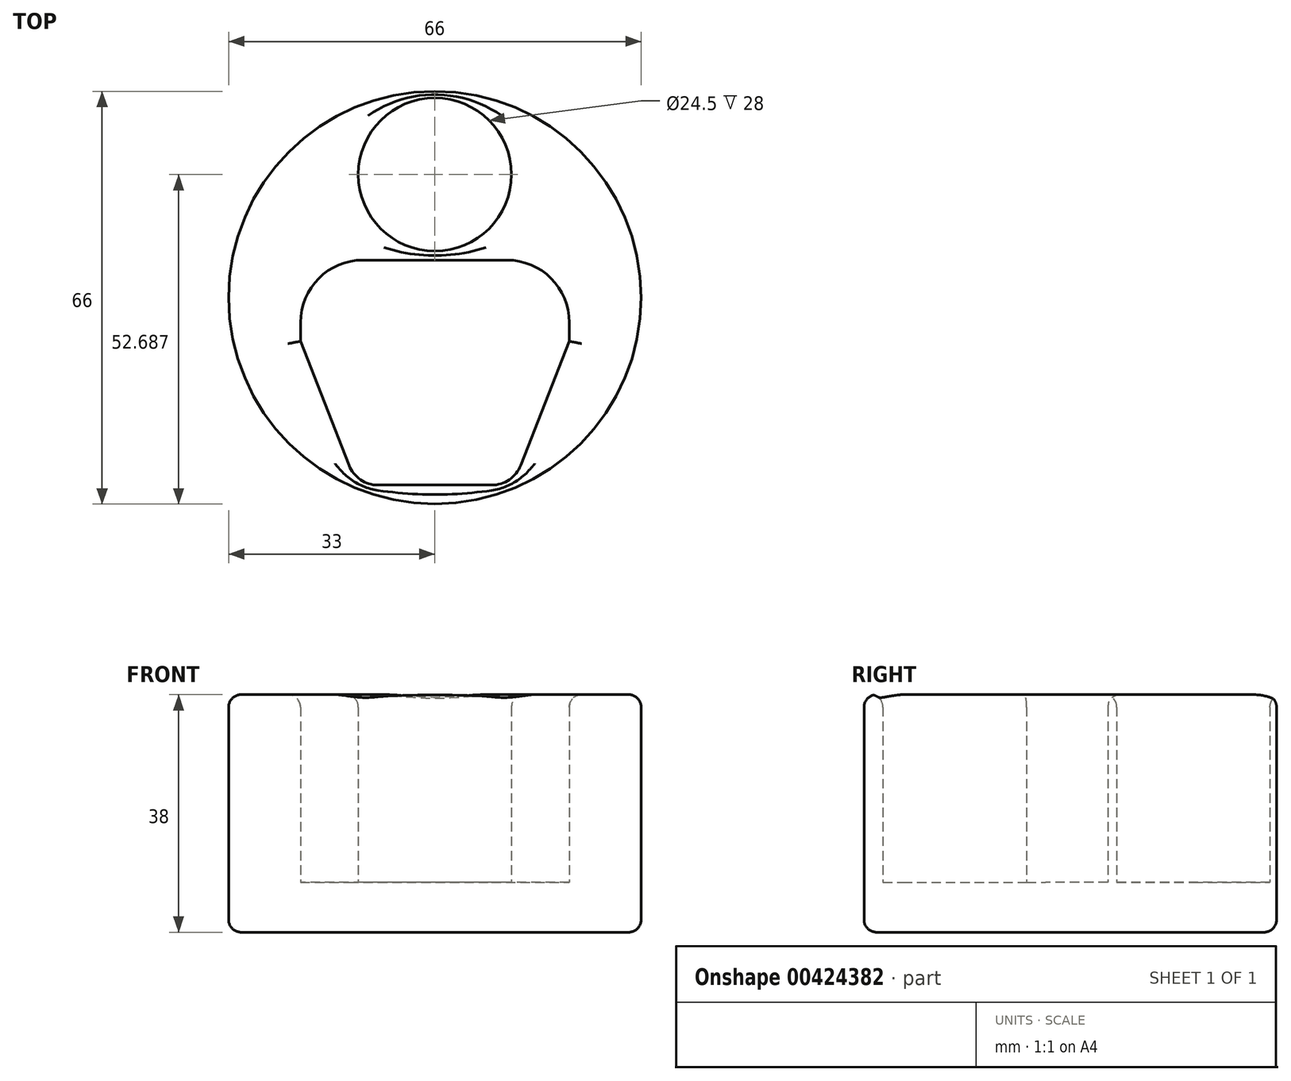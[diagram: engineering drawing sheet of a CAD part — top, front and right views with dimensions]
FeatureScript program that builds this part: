
annotation { "Feature Type Name" : "Feature", "Feature Type Description" : "" }
export const myFeature = defineFeature(function(context is Context, id is Id, definition is map)
    precondition{}
    {
        {
            var Q0;
            Q0=qCreatedBy(makeId("Top.planeOp"),FACE);
            var sketch = newSketch(context, id + "F0", { "sketchPlane" : qUnion([Q0])});
            skCircle(sketch, "E0", {"center": v(0, 0) * mm, "radius": 33 * mm});
            skCircle(sketch, "E1", {"center": v(0, 19.69) * mm, "radius": 12.25 * mm});
            skLineSegment(sketch, "E2", {"start": v(-9.09, -29.99) * mm, "end": v(9.09, -29.99) * mm});
            skLineSegment(sketch, "E3", {"start": v(13.74, -26.81) * mm, "end": v(21.5, -6.99) * mm});
            skLineSegment(sketch, "E4", {"start": v(21.5, -6.99) * mm, "end": v(21.5, -3.99) * mm});
            skLineSegment(sketch, "E5", {"start": v(11.5, 6.01) * mm, "end": v(-11.5, 6.01) * mm});
            skLineSegment(sketch, "E6", {"start": v(-21.5, -3.99) * mm, "end": v(-21.5, -6.99) * mm});
            skLineSegment(sketch, "E7", {"start": v(-21.5, -6.99) * mm, "end": v(-13.74, -26.81) * mm});
            skPoint(sketch, "E8.visualSharp", {"position": v(21.5, 6.01) * mm});
            skArc(sketch, "E8.filletArc", {"start": v(21.5, -3.99) * mm, "mid": v(18.57, 3.08) * mm, "end": v(11.5, 6.01) * mm});
            skArc(sketch, "E9.filletArc", {"start": v(-11.5, 6.01) * mm, "mid": v(-18.57, 3.08) * mm, "end": v(-21.5, -3.99) * mm});
            skPoint(sketch, "E10.visualSharp", {"position": v(12.5, -29.99) * mm});
            skArc(sketch, "E10.filletArc", {"start": v(9.09, -29.99) * mm, "mid": v(11.9, -29.12) * mm, "end": v(13.74, -26.81) * mm});
            skPoint(sketch, "E11.visualSharp", {"position": v(-12.5, -29.99) * mm});
            skArc(sketch, "E11.filletArc", {"start": v(-13.74, -26.81) * mm, "mid": v(-11.9, -29.12) * mm, "end": v(-9.09, -29.99) * mm});
            skLineSegment(sketch, "E12", {"start": v(0, 11.72) * mm, "end": v(0, -22.8) * mm, "construction": true});
            skSolve(sketch);
        }
        {
            var Q0;
            Q0=makeQuery(id+"F0.imprint","IMPRINT",FACE,{"disambiguationData":[TD([[makeQuery(id+"F0.imprint","IMPRINT",EDGE,{"derivedFrom":sQuery(id+"F0.wireOp",EDGE,"E0")}),1.0]])]});
            var Q1;
            Q1 = qSketchRegion(id + "F2", true);
            extrude(context, id + "F1", {"entities" : qUnion([Q0, Q1]), "depth" : 30 * mm});
        }
        {
            var Q0;
            Q0=makeQuery(id+"F0.imprint","IMPRINT",FACE,{"disambiguationData":[TD([[makeQuery(id+"F0.imprint","IMPRINT",EDGE,{"derivedFrom":sQuery(id+"F0.wireOp",EDGE,"E0")}),1.0]])]});
            var sketch = newSketch(context, id + "F2", { "sketchPlane" : qUnion([Q0])});
            skCircle(sketch, "E13", {"center": v(0, 0) * mm, "radius": 33 * mm});
            skSolve(sketch);
        }
        {
            var Q0;
            Q0 = qSketchRegion(id + "F2", true);
            extrude(context, id + "F3", {"entities" : qUnion([Q0]), "operationType" : NewBodyOperationType.ADD, "oppositeDirection" : true, "depth" : 8 * mm});
        }
        {
            var Q0;
            Q0=makeQuery(id+"F1.opExtrude","CAP_EDGE",EDGE,{"disambiguationData":[OSD([sQuery(id+"F0.wireOp",EDGE,"E0")])],"isStart":false});
            var Q1;
            Q1=makeQuery(id+"F3.opExtrude","CAP_EDGE",EDGE,{"disambiguationData":[OSD([sQuery(id+"F2.wireOp",EDGE,"E13")])],"isStart":false});
            var Q2;
            Q2=makeQuery(id+"F1.opExtrude","CAP_EDGE",EDGE,{"disambiguationData":[OSD([sQuery(id+"F0.wireOp",EDGE,"E1")])],"isStart":false});
            var Q3;
            Q3=makeQuery(id+"F1.opExtrude","CAP_EDGE",EDGE,{"disambiguationData":[OSD([sQuery(id+"F0.wireOp",EDGE,"E9.filletArc")])],"isStart":false});
            var Q4;
            Q4=makeQuery(id+"F1.opExtrude","CAP_EDGE",EDGE,{"disambiguationData":[OSD([sQuery(id+"F0.wireOp",EDGE,"E5")])],"isStart":false});
            var Q5;
            Q5=makeQuery(id+"F1.opExtrude","CAP_EDGE",EDGE,{"disambiguationData":[OSD([sQuery(id+"F0.wireOp",EDGE,"E3")])],"isStart":false});
            var Q6;
            Q6=makeQuery(id+"F1.opExtrude","CAP_EDGE",EDGE,{"disambiguationData":[OSD([sQuery(id+"F0.wireOp",EDGE,"E2")])],"isStart":false});
            fillet(context, id + "F4", {"entities" : qUnion([Q0, Q1, Q2, Q3, Q4, Q5, Q6]), "radius" : 2 * mm, "tangentPropagation" : true, "allowEdgeOverflow" : false});
        }
    });
